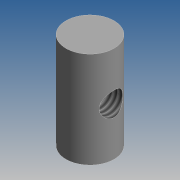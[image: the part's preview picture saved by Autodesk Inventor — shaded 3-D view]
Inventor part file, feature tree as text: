
AUTODESK INVENTOR PART (.ipt)
format: ipt  version: 2019 (Build 230136000, 136)  size: 199,680 bytes
history: native  units: mm
features: sketch x2, extrude x1, plane x1, hole x1
ambient origin geometry x8: Origin, YZ Plane, XZ Plane, XY Plane, X Axis, Y Axis, Z Axis, Center Point
bodies: Solid1 (feature_tree)
feature tree (5):
  extrude  "Extrusion1"  Depth=10.0mm TaperAngle=0.0deg
  plane  "Work Plane1"
  hole  "Hole1"  [1 undecoded]
  sketch  "Sketch1"  dims[d0=5.0mm d1=10.0mm d2=0.0mm]
  sketch  "Sketch3"  dims[d3=3.0mm d4=2.459mm d5=6.0mm d6=4.0mm d7=2.0mm d8=90.0deg d9=8.8mm d10=20.594885mm]
note: 1 required parameter value undecoded (feature->parameter linkage not recoverable at this tier; creation-order binding heuristic only, values carry confidence <= 0.55)
